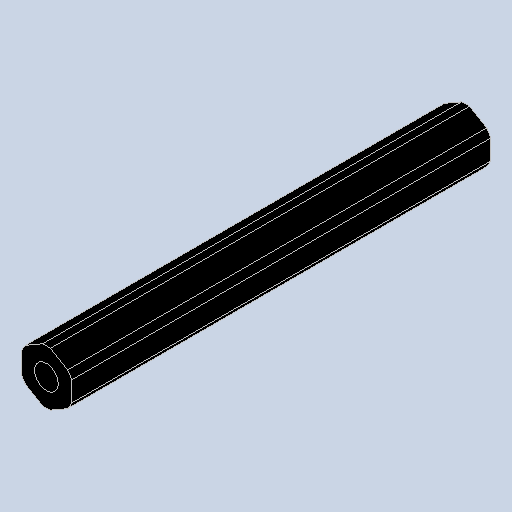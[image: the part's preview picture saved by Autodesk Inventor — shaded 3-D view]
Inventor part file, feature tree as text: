
AUTODESK INVENTOR PART (.ipt)
format: ipt  version: 2023.4 (Build 274418000, 418)  size: 258,048 bytes
history: native  units: in
note: dims shown in document units (in); Inventor stores cm internally (conversion verified against a paired STEP export)
features: extrude x2, projected_geometry x2, hole x1
ambient origin geometry x8: Origin, YZ Plane, XZ Plane, XY Plane, X Axis, Y Axis, Z Axis, Center Point
bodies: Solid1 (feature_tree)
feature tree (5):
  extrude  "Extrusion1"  TaperAngle=0.0deg  [1 undecoded]
  hole  "Hole1"  [1 undecoded]
  extrude  "Extrusion3"  TaperAngle=0.0deg  [1 undecoded]
  projected_geometry  "Project Cut Edges1"
  projected_geometry  "Project Cut Edges2"
note: 3 required parameter values undecoded (feature->parameter linkage not recoverable at this tier; creation-order binding heuristic only, values carry confidence <= 0.55)
